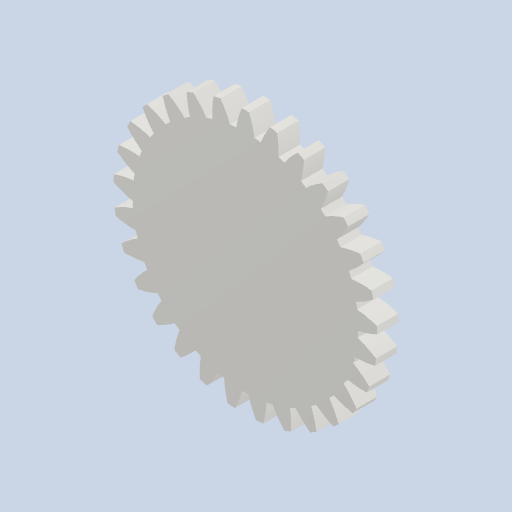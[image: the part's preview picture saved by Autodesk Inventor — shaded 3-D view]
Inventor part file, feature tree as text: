
AUTODESK INVENTOR PART (.ipt)
format: ipt  version: 2022 (Build 260153000, 153)  size: 252,416 bytes
history: native  units: mm (DEFAULTED — no unit token found)
features: plane x3, other x3, sketch x2, extrude x1
ambient origin geometry x8: Origin, YZ Plane, XZ Plane, XY Plane, X Axis, Y Axis, Z Axis, Center Point
bodies: Solid1 (feature_tree)
feature tree (9):
  extrude  "Extrusion1"  Depth=5.0mm TaperAngle=0.0deg
  plane  "Work Plane2"
  plane  "Work Plane8"
  plane  "Work Plane9"
  other  "Цилиндрическое зубчатое зацепление"
  sketch  "Sketch1"  dims[d0=61.999458mm d1=5.0mm d2=0.0mm]
  sketch  "Sketch2"  dims[d3=58.0mm d4=10.0mm d5=0.0mm d16=40.945848mm d17=0.0mm d34=1.083308mm d39=0.0mm d41=0.0mm d43=40.945848mm d46=40.945848mm d47=0.0mm d48=0.0mm]
  other  "Srf1"
  other  "Средний диаметр"
